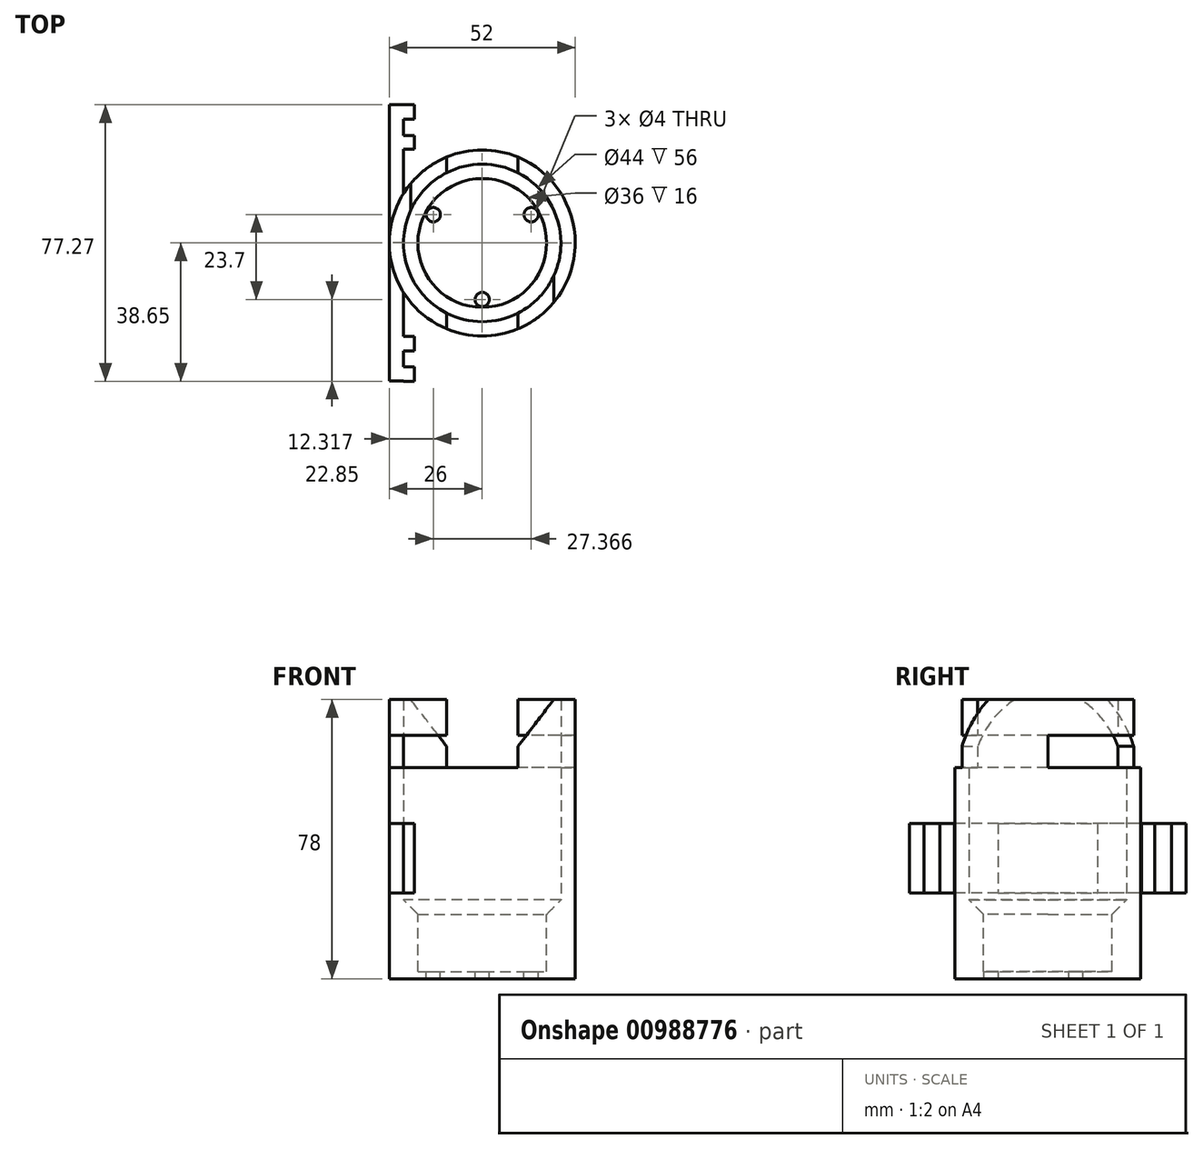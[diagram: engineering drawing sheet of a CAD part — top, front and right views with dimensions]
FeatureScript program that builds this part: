
annotation { "Feature Type Name" : "Feature", "Feature Type Description" : "" }
export const myFeature = defineFeature(function(context is Context, id is Id, definition is map)
    precondition{}
    {
        {
            var Q0;
            Q0=qCreatedBy(makeId("Top.planeOp"),FACE);
            var sketch = newSketch(context, id + "F0", { "sketchPlane" : qUnion([Q0])});
            skCircle(sketch, "E0", {"center": v(0, 0) * mm, "radius": 22 * mm});
            skCircle(sketch, "E1.0", {"center": v(0, 0) * mm, "radius": 26 * mm});
            skSolve(sketch);
        }
        {
            var Q0;
            Q0 = qSketchRegion(id + "F0", true);
            extrude(context, id + "F1", {"entities" : qUnion([Q0]), "depth" : 37 * mm, "offsetDistance" : 25 * mm});
        }
        {
            var Q0;
            Q0=makeQuery(id+"F1.opExtrude","CAP_FACE",FACE,{"disambiguationData":[OSD([sQuery(id+"F0.wireOp",EDGE,"E0"),sQuery(id+"F0.wireOp",EDGE,"E1.0")])],"isStart":true});
            var sketch = newSketch(context, id + "F2", { "sketchPlane" : qUnion([Q0])});
            skCircle(sketch, "E2", {"center": v(0, 0) * mm, "radius": 18 * mm});
            skCircle(sketch, "E3.0", {"center": v(0, 0) * mm, "radius": 26 * mm});
            skSolve(sketch);
        }
        {
            var Q0;
            Q0 = qSketchRegion(id + "F2", true);
            extrude(context, id + "F3", {"entities" : qUnion([Q0]), "operationType" : NewBodyOperationType.ADD, "depth" : 20 * mm, "offsetDistance" : 25 * mm});
        }
        {
            var Q0;
            Q0=makeQuery(id+"F3.opExtrude","CAP_FACE",FACE,{"disambiguationData":[OSD([sQuery(id+"F2.wireOp",EDGE,"E2"),sQuery(id+"F2.wireOp",EDGE,"E3.0")])],"isStart":false});
            var sketch = newSketch(context, id + "F4", { "sketchPlane" : qUnion([Q0])});
            skCircle(sketch, "E4", {"center": v(0, 0) * mm, "radius": 26 * mm});
            skCircle(sketch, "E5", {"center": v(0, 15.8) * mm, "radius": 2 * mm});
            skCircle(sketch, "E6", {"center": v(-13.68, -7.9) * mm, "radius": 2 * mm});
            skCircle(sketch, "E7", {"center": v(13.68, -7.9) * mm, "radius": 2 * mm});
            skSolve(sketch);
        }
        {
            var Q0;
            Q0 = qSketchRegion(id + "F4", true);
            extrude(context, id + "F5", {"entities" : qUnion([Q0]), "operationType" : NewBodyOperationType.ADD, "depth" : 2 * mm, "offsetDistance" : 25 * mm});
        }
        {
            var Q0;
            Q0=makeQuery(id+"F1.opExtrude","CAP_FACE",FACE,{"disambiguationData":[OSD([sQuery(id+"F0.wireOp",EDGE,"E0"),sQuery(id+"F0.wireOp",EDGE,"E1.0")])],"isStart":false});
            var sketch = newSketch(context, id + "F6", { "sketchPlane" : qUnion([Q0])});
            skArc(sketch, "E8", {"start": v(-10, 24) * mm, "mid": v(-26, 0) * mm, "end": v(-10, -24) * mm});
            skArc(sketch, "E9.0", {"start": v(-10, 19.6) * mm, "mid": v(-22, 0) * mm, "end": v(-10, -19.6) * mm});
            skLineSegment(sketch, "E10.left", {"start": v(-10, -24) * mm, "end": v(-10, -19.6) * mm});
            skLineSegment(sketch, "E10.right", {"start": v(10, -24) * mm, "end": v(10, -19.6) * mm});
            skLineSegment(sketch, "E11.trimOffspring", {"start": v(-10, 19.6) * mm, "end": v(-10, 24) * mm});
            skLineSegment(sketch, "E12.trimOffspring", {"start": v(10, 19.6) * mm, "end": v(10, 24) * mm});
            skArc(sketch, "E13.trimOffspring", {"start": v(10, -19.6) * mm, "mid": v(22, 0) * mm, "end": v(10, 19.6) * mm});
            skArc(sketch, "E14.trimOffspring", {"start": v(10, -24) * mm, "mid": v(26, 0) * mm, "end": v(10, 24) * mm});
            skSolve(sketch);
        }
        {
            var Q0;
            Q0 = qSketchRegion(id + "F6", true);
            extrude(context, id + "F7", {"entities" : qUnion([Q0]), "operationType" : NewBodyOperationType.ADD, "depth" : 19 * mm, "offsetDistance" : 25 * mm});
        }
        {
            var Q0;
            {var subQ0=sQuery(id+"F0.wireOp",EDGE,"E1.0");var subQ1=sQuery(id+"F0.wireOp",EDGE,"E0");Q0=makeQuery(id+"F7.boolean.opBoolean","SPLIT",FACE,{"disambiguationData":[TD([makeQuery(id+"F7.opExtrude","SWEPT_FACE",FACE,{"disambiguationData":[OSD([sQuery(id+"F6.wireOp",EDGE,"E10.left")])]})])],"derivedFrom":makeQuery(id+"F1.opExtrude","CAP_FACE",FACE,{"disambiguationData":[OSD([subQ1,subQ0])],"isStart":false})});}
            var sketch = newSketch(context, id + "F8", { "sketchPlane" : qUnion([Q0])});
            skLineSegment(sketch, "E15.bottom", {"start": v(0, 0) * mm, "end": v(45.6, 0) * mm});
            skLineSegment(sketch, "E15.top", {"start": v(0, 26.9) * mm, "end": v(45.6, 26.9) * mm});
            skLineSegment(sketch, "E15.left", {"start": v(0, 0) * mm, "end": v(0, 26.9) * mm});
            skLineSegment(sketch, "E15.right", {"start": v(45.6, 0) * mm, "end": v(45.6, 26.9) * mm});
            skLineSegment(sketch, "E16.bottom", {"start": v(0, 0) * mm, "end": v(-43.3, 0) * mm});
            skLineSegment(sketch, "E16.top", {"start": v(0, -33.09) * mm, "end": v(-43.3, -33.09) * mm});
            skLineSegment(sketch, "E16.left", {"start": v(0, 0) * mm, "end": v(0, -33.09) * mm});
            skLineSegment(sketch, "E16.right", {"start": v(-43.3, 0) * mm, "end": v(-43.3, -33.09) * mm});
            skSolve(sketch);
        }
        {
            var Q0;
            Q0 = qSketchRegion(id + "F8", true);
            extrude(context, id + "F9", {"entities" : qUnion([Q0]), "operationType" : NewBodyOperationType.REMOVE, "depth" : 9 * mm, "offsetDistance" : 25 * mm});
        }
        {
            var Q0;
            Q0=makeQuery(id+"F3.opExtrude","CAP_EDGE",EDGE,{"disambiguationData":[OSD([sQuery(id+"F2.wireOp",EDGE,"E2")])],"isStart":true});
            chamfer(context, id + "F10", {"entities" : qUnion([Q0]), "width" : 4 * mm, "tangentPropagation" : true});
        }
        {
            var Q0;
            Q0=makeQuery(id+"F7.opExtrude","CAP_EDGE",EDGE,{"disambiguationData":[OSD([sQuery(id+"F6.wireOp",EDGE,"E11.trimOffspring")])],"isStart":false});
            chamfer(context, id + "F11", {"entities" : qUnion([Q0]), "chamferType" : ChamferType.TWO_OFFSETS, "width1" : 10 * mm, "oppositeDirection" : false, "width2" : 13 * mm, "tangentPropagation" : true});
        }
        {
            var Q0;
            Q0=makeQuery(id+"F7.opExtrude","CAP_EDGE",EDGE,{"disambiguationData":[OSD([sQuery(id+"F6.wireOp",EDGE,"E10.right")])],"isStart":false});
            chamfer(context, id + "F12", {"entities" : qUnion([Q0]), "chamferType" : ChamferType.TWO_OFFSETS, "width1" : 13 * mm, "oppositeDirection" : false, "width2" : 10 * mm, "tangentPropagation" : true});
        }
        {
            var Q0;
            Q0=makeQuery(id+"F9.boolean.opBoolean","INTERSECT",EDGE,{"derivedFrom":[makeQuery(id+"F7.boolean.opBoolean","MERGE",FACE,{"derivedFrom":[makeQuery(id+"F5.boolean.opBoolean","MERGE",FACE,{"derivedFrom":[makeQuery(id+"F3.boolean.opBoolean","MERGE",FACE,{"derivedFrom":[makeQuery(id+"F1.opExtrude","SWEPT_FACE",FACE,{"disambiguationData":[OSD([sQuery(id+"F0.wireOp",EDGE,"E1.0")])]}),makeQuery(id+"F3.opExtrude","SWEPT_FACE",FACE,{"disambiguationData":[OSD([sQuery(id+"F2.wireOp",EDGE,"E3.0")])]})]}),makeQuery(id+"F5.opExtrude","SWEPT_FACE",FACE,{"disambiguationData":[OSD([sQuery(id+"F4.wireOp",EDGE,"E4")])]})]}),makeQuery(id+"F7.opExtrude","SWEPT_FACE",FACE,{"disambiguationData":[OSD([sQuery(id+"F6.wireOp",EDGE,"E8")])]}),makeQuery(id+"F7.opExtrude","SWEPT_FACE",FACE,{"disambiguationData":[OSD([sQuery(id+"F6.wireOp",EDGE,"E14.trimOffspring")])]})]}),makeQuery(id+"F9.opExtrude","SWEPT_FACE",FACE,{"disambiguationData":[OSD([sQuery(id+"F8.wireOp",EDGE,"E16.bottom")])]})]});
            var Q1;
            Q1=makeQuery(id+"F9.boolean.opBoolean","INTERSECT",EDGE,{"derivedFrom":[makeQuery(id+"F7.boolean.opBoolean","MERGE",FACE,{"derivedFrom":[makeQuery(id+"F5.boolean.opBoolean","MERGE",FACE,{"derivedFrom":[makeQuery(id+"F3.boolean.opBoolean","MERGE",FACE,{"derivedFrom":[makeQuery(id+"F1.opExtrude","SWEPT_FACE",FACE,{"disambiguationData":[OSD([sQuery(id+"F0.wireOp",EDGE,"E1.0")])]}),makeQuery(id+"F3.opExtrude","SWEPT_FACE",FACE,{"disambiguationData":[OSD([sQuery(id+"F2.wireOp",EDGE,"E3.0")])]})]}),makeQuery(id+"F5.opExtrude","SWEPT_FACE",FACE,{"disambiguationData":[OSD([sQuery(id+"F4.wireOp",EDGE,"E4")])]})]}),makeQuery(id+"F7.opExtrude","SWEPT_FACE",FACE,{"disambiguationData":[OSD([sQuery(id+"F6.wireOp",EDGE,"E8")])]}),makeQuery(id+"F7.opExtrude","SWEPT_FACE",FACE,{"disambiguationData":[OSD([sQuery(id+"F6.wireOp",EDGE,"E14.trimOffspring")])]})]}),makeQuery(id+"F9.opExtrude","CAP_FACE",FACE,{"disambiguationData":[OSD([sQuery(id+"F8.wireOp",EDGE,"E16.bottom"),sQuery(id+"F8.wireOp",EDGE,"E16.top"),sQuery(id+"F8.wireOp",EDGE,"E16.left"),sQuery(id+"F8.wireOp",EDGE,"E16.right")])],"isStart":true})]});
            cPlane(context, id + "F13", {"entities" : qUnion([Q0, Q1]), "cplaneType" : CPlaneType.LINE_ANGLE, "offset" : 25 * mm, "angle" : 90 * degree, "width" : 150 * mm, "height" : 150 * mm});
        }
        {
            var Q0;
            Q0=qCreatedBy(id+"F13.planeOp",FACE);
            var sketch = newSketch(context, id + "F14", { "sketchPlane" : qUnion([Q0])});
            skLineSegment(sketch, "E17.bottom", {"start": v(-38.62, 1.92) * mm, "end": v(38.62, 1.92) * mm});
            skLineSegment(sketch, "E17.top", {"start": v(-38.62, 21.43) * mm, "end": v(38.62, 21.43) * mm});
            skLineSegment(sketch, "E17.left", {"start": v(-38.62, 1.92) * mm, "end": v(-38.62, 21.43) * mm});
            skLineSegment(sketch, "E17.right", {"start": v(38.62, 1.92) * mm, "end": v(38.62, 21.43) * mm});
            skPoint(sketch, "E17.middle", {"position": v(0, 11.67) * mm});
            skSolve(sketch);
        }
        {
            var Q0;
            Q0 = qSketchRegion(id + "F14", true);
            extrude(context, id + "F15", {"entities" : qUnion([Q0]), "operationType" : NewBodyOperationType.ADD, "oppositeDirection" : true, "depth" : 4 * mm, "offsetDistance" : 25 * mm});
        }
        {
            var Q0;
            {var subQ0=sQuery(id+"F14.wireOp",EDGE,"E17.bottom");var subQ1=sQuery(id+"F14.wireOp",EDGE,"E17.top");var subQ2=sQuery(id+"F14.wireOp",EDGE,"E17.left");Q0=makeQuery(id+"F15.boolean.opBoolean","SPLIT",FACE,{"disambiguationData":[TD([makeQuery(id+"F15.opExtrude","SWEPT_FACE",FACE,{"disambiguationData":[OSD([subQ2])]})])],"derivedFrom":makeQuery(id+"F15.opExtrude","CAP_FACE",FACE,{"disambiguationData":[OSD([subQ0,subQ1,subQ2,sQuery(id+"F14.wireOp",EDGE,"E17.right")])],"isStart":false})});}
            var sketch = newSketch(context, id + "F16", { "sketchPlane" : qUnion([Q0])});
            skLineSegment(sketch, "E18.bottom", {"start": v(38.62, 21.43) * mm, "end": v(34.62, 21.43) * mm});
            skLineSegment(sketch, "E18.top", {"start": v(38.62, 1.92) * mm, "end": v(34.62, 1.92) * mm});
            skLineSegment(sketch, "E18.left", {"start": v(38.62, 21.43) * mm, "end": v(38.62, 1.92) * mm});
            skLineSegment(sketch, "E18.right", {"start": v(34.62, 21.43) * mm, "end": v(34.62, 1.92) * mm});
            skLineSegment(sketch, "E19.bottom", {"start": v(29.95, 21.43) * mm, "end": v(26.24, 21.43) * mm});
            skLineSegment(sketch, "E19.top", {"start": v(29.95, 1.92) * mm, "end": v(26.24, 1.92) * mm});
            skLineSegment(sketch, "E19.left", {"start": v(29.95, 21.43) * mm, "end": v(29.95, 1.92) * mm});
            skLineSegment(sketch, "E19.right", {"start": v(26.24, 21.43) * mm, "end": v(26.24, 1.92) * mm});
            skLineSegment(sketch, "E20.bottom", {"start": v(-38.65, 21.43) * mm, "end": v(-34.65, 21.43) * mm});
            skLineSegment(sketch, "E20.top", {"start": v(-38.65, 1.92) * mm, "end": v(-34.65, 1.92) * mm});
            skLineSegment(sketch, "E20.left", {"start": v(-38.65, 21.43) * mm, "end": v(-38.65, 1.92) * mm});
            skLineSegment(sketch, "E20.right", {"start": v(-34.65, 21.43) * mm, "end": v(-34.65, 1.92) * mm});
            skLineSegment(sketch, "E21.bottom", {"start": v(-30.15, 21.43) * mm, "end": v(-26.15, 21.43) * mm});
            skLineSegment(sketch, "E21.top", {"start": v(-30.15, 1.92) * mm, "end": v(-26.15, 1.92) * mm});
            skLineSegment(sketch, "E21.left", {"start": v(-30.15, 21.43) * mm, "end": v(-30.15, 1.92) * mm});
            skLineSegment(sketch, "E21.right", {"start": v(-26.15, 21.43) * mm, "end": v(-26.15, 1.92) * mm});
            skSolve(sketch);
        }
        {
            var Q0;
            Q0 = qSketchRegion(id + "F16", true);
            extrude(context, id + "F17", {"entities" : qUnion([Q0]), "operationType" : NewBodyOperationType.ADD, "depth" : 3 * mm, "offsetDistance" : 25 * mm});
        }
    });
